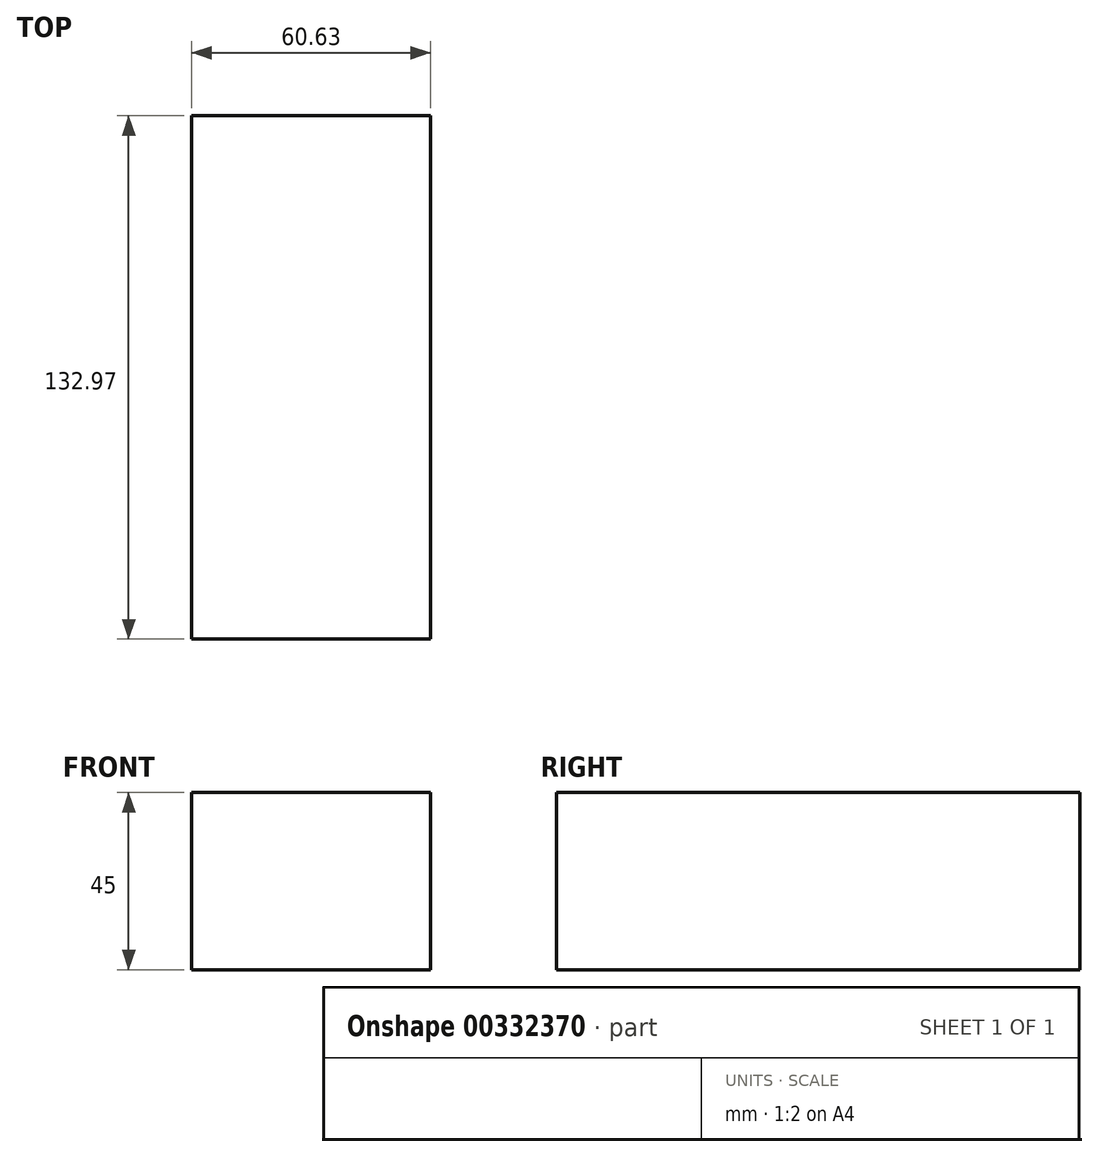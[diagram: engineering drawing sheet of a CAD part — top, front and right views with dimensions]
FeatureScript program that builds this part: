
annotation { "Feature Type Name" : "Feature", "Feature Type Description" : "" }
export const myFeature = defineFeature(function(context is Context, id is Id, definition is map)
    precondition{}
    {
        {
            var Q0;
            Q0=qCreatedBy(makeId("Top.planeOp"),FACE);
            var sketch = newSketch(context, id + "F0", { "sketchPlane" : qUnion([Q0])});
            skLineSegment(sketch, "E0.bottom", {"start": v(0, -58.18) * mm, "end": v(-60.63, -58.18) * mm});
            skLineSegment(sketch, "E0.top", {"start": v(0, 74.8) * mm, "end": v(-60.63, 74.8) * mm});
            skLineSegment(sketch, "E0.left", {"start": v(0, -58.18) * mm, "end": v(0, 74.8) * mm});
            skLineSegment(sketch, "E0.right", {"start": v(-60.63, -58.18) * mm, "end": v(-60.63, 74.8) * mm});
            skSolve(sketch);
        }
        {
            var Q0;
            Q0=makeQuery(id+"F0.imprint","IMPRINT",FACE,{"disambiguationData":[TD([[makeQuery(id+"F0.imprint","IMPRINT",EDGE,{"derivedFrom":sQuery(id+"F0.wireOp",EDGE,"E0.bottom")}),-1.0]])]});
            extrude(context, id + "F1", {"entities" : qUnion([Q0]), "depth" : 45 * mm});
        }
        {
            var Q0;
            Q0=makeQuery(id+"F1.opExtrude","CAP_FACE",FACE,{"disambiguationData":[OSD([sQuery(id+"F0.wireOp",EDGE,"E0.bottom"),sQuery(id+"F0.wireOp",EDGE,"E0.top"),sQuery(id+"F0.wireOp",EDGE,"E0.left"),sQuery(id+"F0.wireOp",EDGE,"E0.right")])],"isStart":false});
            var sketch = newSketch(context, id + "F2", { "sketchPlane" : qUnion([Q0])});
            skLineSegment(sketch, "E1.bottom", {"start": v(-50.03, -9.96) * mm, "end": v(0, -9.96) * mm});
            skLineSegment(sketch, "E1.top", {"start": v(-50.03, 27.54) * mm, "end": v(0, 27.54) * mm});
            skLineSegment(sketch, "E1.left", {"start": v(-50.03, -9.96) * mm, "end": v(-50.03, 27.54) * mm});
            skLineSegment(sketch, "E1.right", {"start": v(0, -9.96) * mm, "end": v(0, 27.54) * mm});
            skSolve(sketch);
        }
        {
            var Q0;
            Q0 = qSketchRegion(id + "F2", true);
            extrude(context, id + "F3", {"entities" : qUnion([Q0]), "operationType" : NewBodyOperationType.ADD, "oppositeDirection" : true, "depth" : 25.4 * mm});
        }
    });
